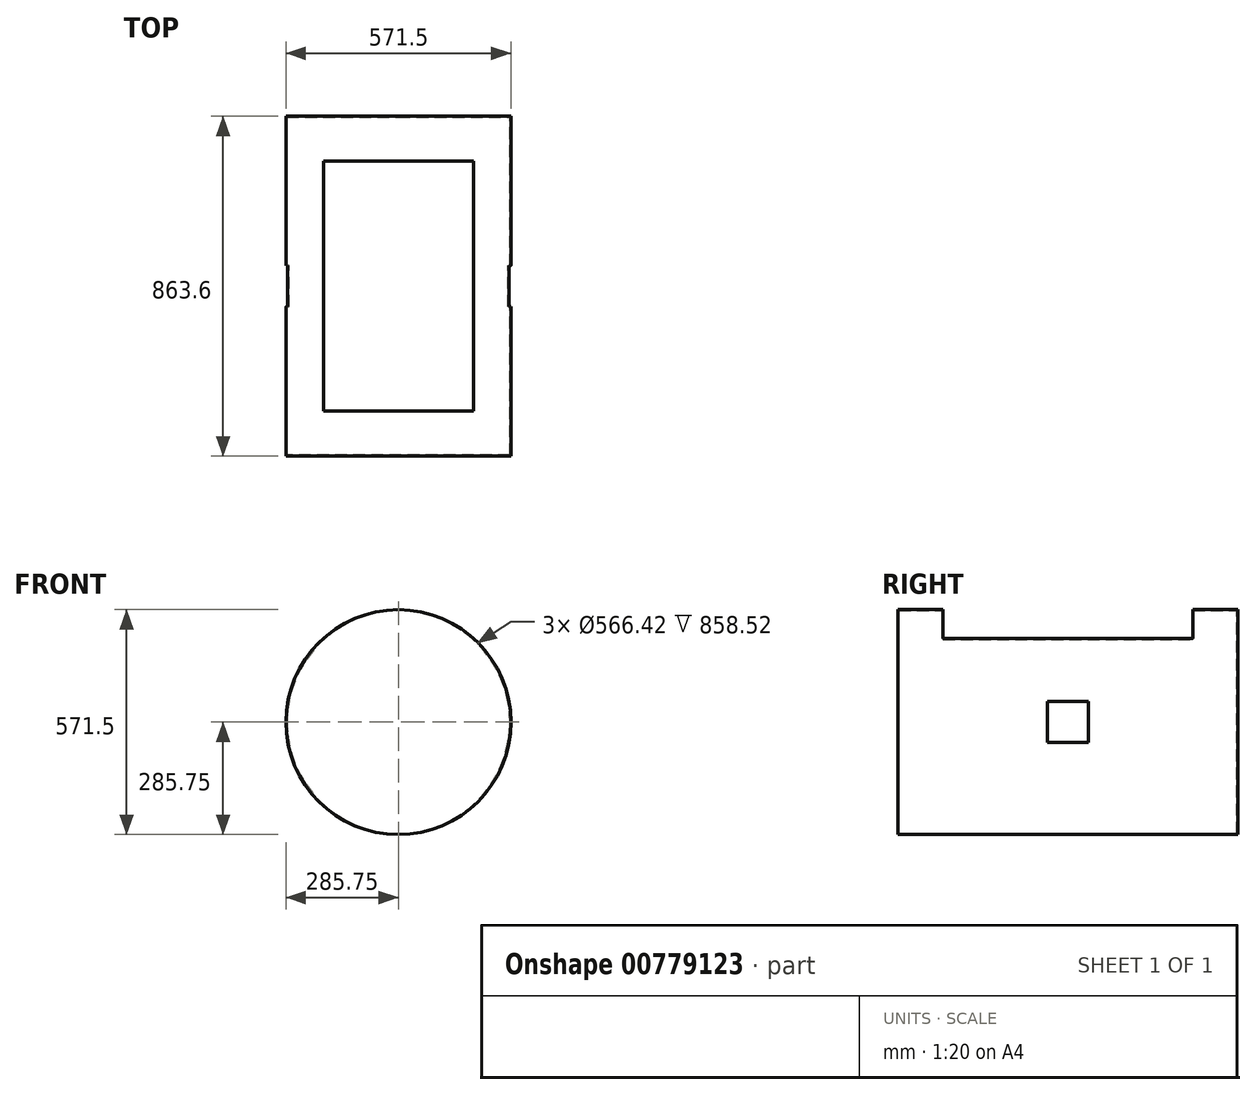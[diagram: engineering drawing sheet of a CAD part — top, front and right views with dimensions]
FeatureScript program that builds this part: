
annotation { "Feature Type Name" : "Feature", "Feature Type Description" : "" }
export const myFeature = defineFeature(function(context is Context, id is Id, definition is map)
    precondition{}
    {
        {
            var Q0;
            Q0=qCreatedBy(makeId("Front.planeOp"),FACE);
            var sketch = newSketch(context, id + "F0", { "sketchPlane" : qUnion([Q0])});
            skCircle(sketch, "E0", {"center": v(0, 0) * mm, "radius": 285.75 * mm});
            skSolve(sketch);
        }
        {
            var Q0;
            Q0=qSketchRegion(id+"F0",true);
            extrude(context, id + "F1", {"entities" : qUnion([Q0]), "endBound" : BoundingType.SYMMETRIC, "depth" : 863.6 * mm, "offsetDistance" : 25.4 * mm});
        }
        {
            var Q0;
            Q0=qCreatedBy(makeId("Top.planeOp"),FACE);
            var sketch = newSketch(context, id + "F2", { "sketchPlane" : qUnion([Q0])});
            skLineSegment(sketch, "E1.bottom", {"start": v(-190.5, 317.5) * mm, "end": v(190.5, 317.5) * mm});
            skLineSegment(sketch, "E1.top", {"start": v(-190.5, -317.5) * mm, "end": v(190.5, -317.5) * mm});
            skLineSegment(sketch, "E1.left", {"start": v(-190.5, 317.5) * mm, "end": v(-190.5, -317.5) * mm});
            skLineSegment(sketch, "E1.right", {"start": v(190.5, 317.5) * mm, "end": v(190.5, -317.5) * mm});
            skPoint(sketch, "E1.middle", {"position": v(0, 0) * mm});
            skSolve(sketch);
        }
        {
            var Q0;
            Q0=qSketchRegion(id+"F2",true);
            extrude(context, id + "F3", {"entities" : qUnion([Q0]), "operationType" : NewBodyOperationType.REMOVE, "depth" : 452.12 * mm, "offsetDistance" : 25.4 * mm});
        }
        {
            var Q0;
            Q0=makeQuery(id+"F3.boolean.opBoolean","COPY",FACE,{"derivedFrom":makeQuery(id+"F3.opExtrude","SWEPT_FACE",FACE,{"disambiguationData":[OSD([sQuery(id+"F2.wireOp",EDGE,"E1.bottom")])]})});
            var Q1;
            Q1=makeQuery(id+"F3.boolean.opBoolean","COPY",FACE,{"derivedFrom":makeQuery(id+"F3.opExtrude","SWEPT_FACE",FACE,{"disambiguationData":[OSD([sQuery(id+"F2.wireOp",EDGE,"E1.left")])]})});
            var Q2;
            Q2=makeQuery(id+"F3.boolean.opBoolean","COPY",FACE,{"derivedFrom":makeQuery(id+"F3.opExtrude","CAP_FACE",FACE,{"disambiguationData":[OSD([sQuery(id+"F2.wireOp",EDGE,"E1.bottom"),sQuery(id+"F2.wireOp",EDGE,"E1.top"),sQuery(id+"F2.wireOp",EDGE,"E1.left"),sQuery(id+"F2.wireOp",EDGE,"E1.right")])],"isStart":true})});
            var Q3;
            Q3=makeQuery(id+"F3.boolean.opBoolean","COPY",FACE,{"derivedFrom":makeQuery(id+"F3.opExtrude","SWEPT_FACE",FACE,{"disambiguationData":[OSD([sQuery(id+"F2.wireOp",EDGE,"E1.top")])]})});
            var Q4;
            Q4=makeQuery(id+"F3.boolean.opBoolean","COPY",FACE,{"derivedFrom":makeQuery(id+"F3.opExtrude","SWEPT_FACE",FACE,{"disambiguationData":[OSD([sQuery(id+"F2.wireOp",EDGE,"E1.right")])]})});
            shell(context, id + "F4", {"entities" : qUnion([Q0, Q1, Q2, Q3, Q4]), "thickness" : 2.54 * mm});
        }
        {
            var Q0;
            Q0=qCreatedBy(makeId("Right.planeOp"),FACE);
            var sketch = newSketch(context, id + "F5", { "sketchPlane" : qUnion([Q0])});
            skLineSegment(sketch, "E2.bottom", {"start": v(52.07, -52.07) * mm, "end": v(-52.07, -52.07) * mm});
            skLineSegment(sketch, "E2.top", {"start": v(52.07, 52.07) * mm, "end": v(-52.07, 52.07) * mm});
            skLineSegment(sketch, "E2.left", {"start": v(52.07, -52.07) * mm, "end": v(52.07, 52.07) * mm});
            skLineSegment(sketch, "E2.right", {"start": v(-52.07, -52.07) * mm, "end": v(-52.07, 52.07) * mm});
            skPoint(sketch, "E2.middle", {"position": v(0, 0) * mm});
            skSolve(sketch);
        }
        {
            var Q0;
            Q0=makeQuery(id+"F5.imprint","IMPRINT",FACE,{"disambiguationData":[TD([[makeQuery(id+"F5.imprint","IMPRINT",EDGE,{"derivedFrom":sQuery(id+"F5.wireOp",EDGE,"E2.bottom")}),-1.0]])]});
            extrude(context, id + "F6", {"entities" : qUnion([Q0]), "operationType" : NewBodyOperationType.REMOVE, "endBound" : BoundingType.THROUGH_ALL, "oppositeDirection" : true, "depth" : 25.4 * mm, "offsetDistance" : 25.4 * mm, "hasSecondDirection" : true, "secondDirectionBound" : SecondDirectionBoundingType.THROUGH_ALL, "secondDirectionOppositeDirection" : false, "secondDirectionDepth" : 25.4 * mm});
        }
    });
